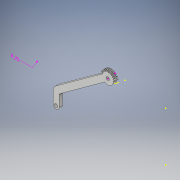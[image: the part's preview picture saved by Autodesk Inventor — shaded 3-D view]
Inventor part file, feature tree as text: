
AUTODESK INVENTOR PART (.ipt)
format: ipt  version: 2018 (Build 220112000, 112)  size: 217,600 bytes
history: native  units: in
note: dims shown in document units (in); Inventor stores cm internally (conversion verified against a paired STEP export)
features: sketch x9, extrude x4, other x2, plane x1, pattern_circular x1
ambient origin geometry x8: Origin, YZ Plane, XZ Plane, XY Plane, X Axis, Y Axis, Z Axis, Center Point
bodies: Solid1 (feature_tree)
feature tree (17):
  other  "Annotations"
  extrude  "Extrusion1"  Depth=0.1181in
  extrude  "Extrusion11"  Depth=0.1969in
  sketch  "Sketch13"  dims[d65=0.1969in d69=0.1094in]
  sketch  "Sketch15"  dims[d70=0.1969in d71=0.1181in]
  sketch  "Sketch16"  dims[d72=0.1969in d73=0.0in]
  plane  "Work Plane2"
  sketch  "Sketch18"  dims[d82=0.0591in]
  extrude  "Extrusion13"  Depth=0.1094in
  sketch  "Sketch20"  dims[d84=0.0098in]
  extrude  "Extrusion15"  Depth=0.1181in
  pattern_circular  "Circular Pattern2"  [2 undecoded]
  sketch  "Sketch1"  dims[d7=0.1181in d8=0.0in d15=1.0in]
  sketch  "Sketch12"  dims[d47=0.1969in d48=0.1969in d63=2.1654in d64=0.1969in]
  sketch  "Sketch19"  dims[d83=0.0197in]
  sketch  "Sketch21"  dims[d85=0.0394in d86=0.0098in d87=0.1181in d88=0.0in d94=0.1181in d95=0.1181in d96=0.0in d97=3.937in d98=-0.9757in d100=0.1094in d103=0.0787in d28=1.2193in d29=0.25in]
  other  "Radial Dimension 1"
note: 2 required parameter values undecoded (feature->parameter linkage not recoverable at this tier; creation-order binding heuristic only, values carry confidence <= 0.55)
